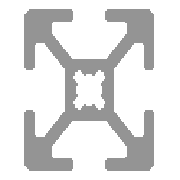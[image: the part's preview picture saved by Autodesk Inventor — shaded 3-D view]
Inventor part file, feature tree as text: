
AUTODESK INVENTOR PART (.ipt)
format: ipt  version: 2017 (Build 210142000, 142)  size: 228,864 bytes
history: native  units: in
note: dims shown in document units (in); Inventor stores cm internally (conversion verified against a paired STEP export)
features: other x3, sketch x1
ambient origin geometry x8: Origin, YZ Plane, XZ Plane, XY Plane, X Axis, Y Axis, Z Axis, Center Point
bodies: Solid1 (feature_tree), Body (feature_tree)
feature tree (4):
  other  "Blocks"
  other  "Start Plane"
  other  "End Plane"
  sketch  "Sketch1"  dims[d2=-0.0in d3=1.0in d4=18.0in d5=0.0in d7=1.0in]
